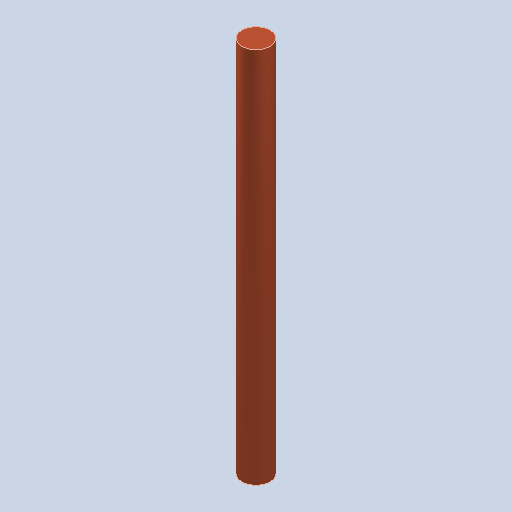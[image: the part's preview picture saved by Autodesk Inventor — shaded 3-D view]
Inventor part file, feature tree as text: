
AUTODESK INVENTOR PART (.ipt)
format: ipt  version: 2024.2 (Build 282272000, 272)  size: 232,960 bytes
history: native  units: mm
features: other x1, extrude x1, sketch x1
ambient origin geometry x8: Origin, YZ Plane, XZ Plane, XY Plane, X Axis, Y Axis, Z Axis, Center Point
bodies: Body1 (feature_tree)
feature tree (3):
  other  "Bryła1"
  extrude  "Wyciągnięcie proste1"  Depth=1.5mm
  sketch  "Szkic1"
